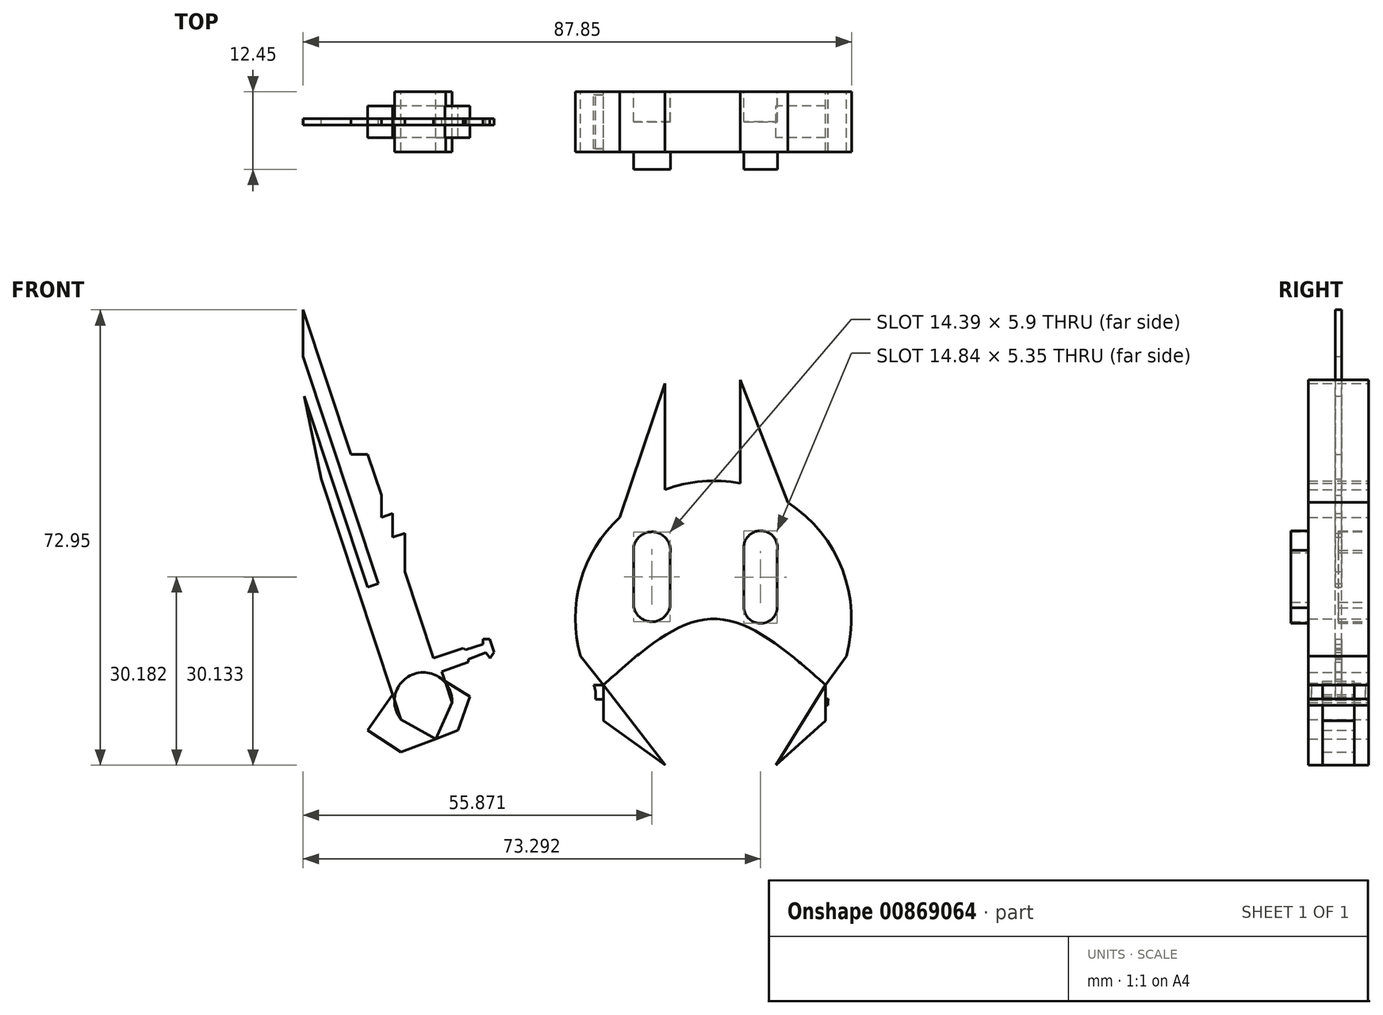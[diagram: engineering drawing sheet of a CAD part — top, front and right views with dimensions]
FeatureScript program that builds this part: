
annotation { "Feature Type Name" : "Feature", "Feature Type Description" : "" }
export const myFeature = defineFeature(function(context is Context, id is Id, definition is map)
    precondition{}
    {
        {
            var Q0;
            Q0=qCreatedBy(makeId("Front.planeOp"),FACE);
            var sketch = newSketch(context, id + "F0", { "sketchPlane" : qUnion([Q0])});
            skLineSegment(sketch, "E0.bottom", {"start": v(-15.76, 7.28) * mm, "end": v(19.82, 7.28) * mm});
            skLineSegment(sketch, "E0.left", {"start": v(-15.76, 7.28) * mm, "end": v(-15.76, 1.57) * mm});
            skLineSegment(sketch, "E0.right", {"start": v(19.82, 7.28) * mm, "end": v(19.82, 1.57) * mm});
            skLineSegment(sketch, "E1", {"start": v(-15.76, 7.28) * mm, "end": v(-19.45, 11.89) * mm});
            skLineSegment(sketch, "E2", {"start": v(23.14, 11.89) * mm, "end": v(19.82, 7.28) * mm});
            skArc(sketch, "E3", {"start": v(23.14, 11.89) * mm, "mid": v(1.84, 40) * mm, "end": v(-19.45, 11.89) * mm});
            skLineSegment(sketch, "E4", {"start": v(-5.9, 38.59) * mm, "end": v(-5.9, 55.58) * mm});
            skLineSegment(sketch, "E5", {"start": v(-5.9, 55.58) * mm, "end": v(-13.15, 34.14) * mm});
            skLineSegment(sketch, "E6", {"start": v(6.13, 39.57) * mm, "end": v(6.13, 56.13) * mm});
            skLineSegment(sketch, "E7", {"start": v(6.13, 56.13) * mm, "end": v(13.75, 36.51) * mm});
            skLineSegment(sketch, "E8", {"start": v(-39.06, 0) * mm, "end": v(-48.21, -3.47) * mm});
            skLineSegment(sketch, "E9", {"start": v(-48.21, -3.47) * mm, "end": v(-53.56, 0) * mm});
            skLineSegment(sketch, "E10", {"start": v(-37.15, 5.44) * mm, "end": v(-39.06, 0) * mm});
            skLineSegment(sketch, "E11", {"start": v(-48.21, 1.77) * mm, "end": v(-60.97, 40.27) * mm});
            skLineSegment(sketch, "E12", {"start": v(-60.97, 40.27) * mm, "end": v(-63.7, 53.56) * mm});
            skLineSegment(sketch, "E13", {"start": v(-63.7, 53.56) * mm, "end": v(-53.56, 22.96) * mm});
            skLineSegment(sketch, "E14", {"start": v(-53.56, 22.96) * mm, "end": v(-51.84, 23.53) * mm});
            skLineSegment(sketch, "E15", {"start": v(-51.84, 23.53) * mm, "end": v(-63.9, 59.88) * mm});
            skLineSegment(sketch, "E16", {"start": v(-63.9, 59.88) * mm, "end": v(-63.9, 67.38) * mm});
            skLineSegment(sketch, "E17", {"start": v(-63.9, 67.38) * mm, "end": v(-57.09, 46.85) * mm});
            skLineSegment(sketch, "E18", {"start": v(-57.09, 46.85) * mm, "end": v(-56.2, 44.2) * mm});
            skLineSegment(sketch, "E19", {"start": v(-56.2, 44.2) * mm, "end": v(-53.56, 44.2) * mm});
            skLineSegment(sketch, "E20", {"start": v(-40.03, 4.48) * mm, "end": v(-41.66, 9.4) * mm});
            skLineSegment(sketch, "E21", {"start": v(-38.25, 13.18) * mm, "end": v(-43.01, 11.6) * mm});
            skLineSegment(sketch, "E22", {"start": v(-43.01, 11.6) * mm, "end": v(-47.6, 25.43) * mm});
            skLineSegment(sketch, "E23", {"start": v(-47.6, 25.43) * mm, "end": v(-47.6, 31.62) * mm});
            skLineSegment(sketch, "E24", {"start": v(-47.6, 31.62) * mm, "end": v(-49.53, 30.98) * mm});
            skLineSegment(sketch, "E25", {"start": v(-49.53, 30.98) * mm, "end": v(-49.53, 34.75) * mm});
            skLineSegment(sketch, "E26", {"start": v(-49.53, 34.75) * mm, "end": v(-51.33, 34.15) * mm});
            skLineSegment(sketch, "E27", {"start": v(-51.33, 34.15) * mm, "end": v(-51.33, 37.7) * mm});
            skLineSegment(sketch, "E28", {"start": v(-51.33, 37.7) * mm, "end": v(-53.56, 44.2) * mm});
            skArc(sketch, "E29", {"start": v(-40.03, 4.48) * mm, "mid": v(-46.08, 9.06) * mm, "end": v(-48.21, 1.77) * mm});
            skLineSegment(sketch, "E30", {"start": v(-42.63, -1.36) * mm, "end": v(-40.03, 4.48) * mm});
            skLineSegment(sketch, "E31", {"start": v(-48.21, 1.77) * mm, "end": v(-42.63, -1.36) * mm});
            skLineSegment(sketch, "E32", {"start": v(-53.56, 0) * mm, "end": v(-49.52, 5.74) * mm});
            skLineSegment(sketch, "E33", {"start": v(-37.15, 5.44) * mm, "end": v(-41.66, 8.2) * mm});
            skArc(sketch, "E34", {"start": v(-10.97, 20.37) * mm, "mid": v(-7.92, 17.42) * mm, "end": v(-5.07, 20.56) * mm});
            skLineSegment(sketch, "E35", {"start": v(-10.97, 20.37) * mm, "end": v(-10.97, 28.85) * mm});
            skLineSegment(sketch, "E36", {"start": v(-5.07, 20.56) * mm, "end": v(-5.07, 28.48) * mm});
            skArc(sketch, "E37", {"start": v(-5.07, 28.48) * mm, "mid": v(-7.82, 31.8) * mm, "end": v(-10.97, 28.85) * mm});
            skArc(sketch, "E38", {"start": v(12.08, 28.85) * mm, "mid": v(9.4, 31.98) * mm, "end": v(6.73, 28.85) * mm});
            skLineSegment(sketch, "E39", {"start": v(6.73, 28.85) * mm, "end": v(6.73, 19.82) * mm});
            skLineSegment(sketch, "E40", {"start": v(12.08, 28.85) * mm, "end": v(12.08, 19.63) * mm});
            skArc(sketch, "E41", {"start": v(6.73, 19.82) * mm, "mid": v(9.31, 17.14) * mm, "end": v(12.08, 19.63) * mm});
            skLineSegment(sketch, "E42", {"start": v(-44.65, -2.12) * mm, "end": v(-42.94, -6.62) * mm});
            skLineSegment(sketch, "E43", {"start": v(-41.24, -0.83) * mm, "end": v(-39.86, -5.04) * mm});
            skCircle(sketch, "E44", {"center": v(-38.9, -10.87) * mm, "radius": 5.92 * mm});
            skCircle(sketch, "E45", {"center": v(-38.9, -10.87) * mm, "radius": 4.33 * mm});
            skCircle(sketch, "E46", {"center": v(-38.9, -10.87) * mm, "radius": 1.05 * mm});
            skFitSpline(sketch, "E47", {"points": [v(-15.76, 7.28) * mm, v(1.84, 17.87) * mm, v(19.82, 7.28) * mm], "startDerivative": vector(35.23, 31.82) * mm, "endDerivative": vector(35.93, -31.74) * mm});
            skCircle(sketch, "E48", {"center": v(-21.52, 5.6) * mm, "radius": 4.51 * mm});
            skLineSegment(sketch, "E49", {"start": v(-15.76, 7.28) * mm, "end": v(-17.33, 7.28) * mm});
            skLineSegment(sketch, "E50", {"start": v(-17.05, 4.97) * mm, "end": v(-15.76, 4.97) * mm});
            skCircle(sketch, "E51", {"center": v(-29.67, -1.68) * mm, "radius": 2.4 * mm});
            skLineSegment(sketch, "E52", {"start": v(-32.06, -1.6) * mm, "end": v(-36.48, -5.47) * mm});
            skLineSegment(sketch, "E53", {"start": v(-29.59, -4.07) * mm, "end": v(-33.65, -8.14) * mm});
            skLineSegment(sketch, "E54", {"start": v(-29.32, 0.7) * mm, "end": v(-25.92, 4.57) * mm});
            skLineSegment(sketch, "E55", {"start": v(-27.31, -1.22) * mm, "end": v(-23.42, 1.5) * mm});
            skCircle(sketch, "E56", {"center": v(-29.67, -1.68) * mm, "radius": 1.75 * mm});
            skCircle(sketch, "E57", {"center": v(-21.52, 5.6) * mm, "radius": 1.75 * mm});
            skLineSegment(sketch, "E58", {"start": v(-21.52, 5.6) * mm, "end": v(-23.27, 5.6) * mm});
            skLineSegment(sketch, "E59", {"start": v(-23.27, 5.6) * mm, "end": v(-28.85, -0.13) * mm});
            skLineSegment(sketch, "E60", {"start": v(-21.52, 5.6) * mm, "end": v(-21.52, 3.85) * mm});
            skLineSegment(sketch, "E61", {"start": v(-21.52, 3.85) * mm, "end": v(-28.06, -1) * mm});
            skLineSegment(sketch, "E62", {"start": v(-38.9, -10.87) * mm, "end": v(-38.9, -9.82) * mm});
            skLineSegment(sketch, "E63", {"start": v(-38.9, -9.82) * mm, "end": v(-31.28, -2.36) * mm});
            skLineSegment(sketch, "E64", {"start": v(-38.9, -10.87) * mm, "end": v(-37.85, -10.87) * mm});
            skLineSegment(sketch, "E65", {"start": v(-37.85, -10.87) * mm, "end": v(-30.38, -3.28) * mm});
            skLineSegment(sketch, "E66", {"start": v(-37.15, 5.44) * mm, "end": v(-32.36, 8.08) * mm});
            skLineSegment(sketch, "E67", {"start": v(-32.36, 8.08) * mm, "end": v(-39.06, 0) * mm});
            skLineSegment(sketch, "E68", {"start": v(-59.26, -0.64) * mm, "end": v(-48.21, -3.47) * mm});
            skLineSegment(sketch, "E69", {"start": v(-53.56, 0) * mm, "end": v(-59.26, -0.64) * mm});
            skLineSegment(sketch, "E70", {"start": v(-38.25, 13.18) * mm, "end": v(-37.87, 12.9) * mm});
            skLineSegment(sketch, "E71", {"start": v(-37.87, 12.9) * mm, "end": v(-35.08, 13.83) * mm});
            skLineSegment(sketch, "E72", {"start": v(-35.08, 13.83) * mm, "end": v(-35.08, 14.65) * mm});
            skLineSegment(sketch, "E73", {"start": v(-35.08, 14.65) * mm, "end": v(-33.97, 14.65) * mm});
            skLineSegment(sketch, "E74", {"start": v(-33.97, 14.65) * mm, "end": v(-33.27, 12.51) * mm});
            skLineSegment(sketch, "E75", {"start": v(-33.27, 12.51) * mm, "end": v(-33.9, 11.6) * mm});
            skLineSegment(sketch, "E76", {"start": v(-33.9, 11.6) * mm, "end": v(-34.63, 12.5) * mm});
            skLineSegment(sketch, "E77", {"start": v(-34.63, 12.5) * mm, "end": v(-37.4, 11.4) * mm});
            skLineSegment(sketch, "E78", {"start": v(-37.4, 11.4) * mm, "end": v(-37.4, 10.98) * mm});
            skLineSegment(sketch, "E79", {"start": v(-37.4, 10.98) * mm, "end": v(-41.66, 9.4) * mm});
            skCircle(sketch, "E80", {"center": v(33.96, -15.69) * mm, "radius": 5 * mm});
            skLineSegment(sketch, "E81", {"start": v(-15.76, 1.57) * mm, "end": v(-5.84, -5.57) * mm});
            skLineSegment(sketch, "E82", {"start": v(-5.84, -5.57) * mm, "end": v(11.89, -5.57) * mm});
            skLineSegment(sketch, "E83", {"start": v(11.89, -5.57) * mm, "end": v(19.82, 1.57) * mm});
            skLineSegment(sketch, "E84", {"start": v(-15.76, 7.28) * mm, "end": v(-5.84, -5.57) * mm});
            skLineSegment(sketch, "E85", {"start": v(19.82, 7.28) * mm, "end": v(11.89, -5.57) * mm});
            skLineSegment(sketch, "E86", {"start": v(25.44, 1.57) * mm, "end": v(25.18, 7.28) * mm});
            skLineSegment(sketch, "E87", {"start": v(-9.91, 12.56) * mm, "end": v(-6, 7.28) * mm});
            skLineSegment(sketch, "E88", {"start": v(13.8, 12.59) * mm, "end": v(9.34, 7.28) * mm});
            skLineSegment(sketch, "E89", {"start": v(25.18, 7.28) * mm, "end": v(30.14, 24.43) * mm});
            skLineSegment(sketch, "E90", {"start": v(30.14, 24.43) * mm, "end": v(32.94, 16.26) * mm});
            skArc(sketch, "E91", {"start": v(32.94, 16.26) * mm, "mid": v(27.23, 9.12) * mm, "end": v(33.8, 2.77) * mm});
            skLineSegment(sketch, "E92", {"start": v(33.8, 2.77) * mm, "end": v(33.8, -2.6) * mm});
            skCircle(sketch, "E93", {"center": v(22.55, 4.35) * mm, "radius": 2.39 * mm});
            skLineSegment(sketch, "E94", {"start": v(24.76, 5.25) * mm, "end": v(25.31, 5.28) * mm});
            skPoint(sketch, "E94.endSnap0", {"position": v(25.31, 4.42) * mm});
            skLineSegment(sketch, "E95", {"start": v(24.9, 3.98) * mm, "end": v(25.33, 4) * mm});
            skLineSegment(sketch, "E96", {"start": v(20.26, 5.03) * mm, "end": v(19.82, 5.03) * mm});
            skLineSegment(sketch, "E97", {"start": v(20.18, 4.02) * mm, "end": v(19.82, 4.02) * mm});
            skLineSegment(sketch, "E98", {"start": v(25.44, 1.57) * mm, "end": v(33.8, -2.6) * mm});
            skCircle(sketch, "E99", {"center": v(34, 9.56) * mm, "radius": 5.31 * mm});
            skLineSegment(sketch, "E100", {"start": v(28.72, 9.03) * mm, "end": v(27.23, 9.03) * mm});
            skLineSegment(sketch, "E101", {"start": v(28.78, 10.5) * mm, "end": v(27.28, 10.5) * mm});
            skArc(sketch, "E102", {"start": v(35.95, 10.39) * mm, "mid": v(34.13, 12.17) * mm, "end": v(32.23, 10.46) * mm});
            skLineSegment(sketch, "E103", {"start": v(32.23, 10.46) * mm, "end": v(32.23, -14.4) * mm});
            skLineSegment(sketch, "E104", {"start": v(32.23, -14.4) * mm, "end": v(33.96, -15.69) * mm});
            skLineSegment(sketch, "E105", {"start": v(33.96, -15.69) * mm, "end": v(35.7, -14.4) * mm});
            skLineSegment(sketch, "E106", {"start": v(35.7, -14.4) * mm, "end": v(35.95, 10.39) * mm});
            skArc(sketch, "E107", {"start": v(32.23, -14.4) * mm, "mid": v(33.96, -18.06) * mm, "end": v(35.7, -14.4) * mm});
            skLineSegment(sketch, "E108", {"start": v(35.2, -20.53) * mm, "end": v(35.2, -28.23) * mm});
            skLineSegment(sketch, "E109", {"start": v(32.87, -20.57) * mm, "end": v(32.87, -28.2) * mm});
            skLineSegment(sketch, "E110", {"start": v(39.5, -25.26) * mm, "end": v(35.95, -41.2) * mm});
            skLineSegment(sketch, "E111", {"start": v(28.5, -25.57) * mm, "end": v(24.97, -22.31) * mm});
            skLineSegment(sketch, "E112", {"start": v(24.97, -22.31) * mm, "end": v(26.4, -28.2) * mm});
            skLineSegment(sketch, "E113", {"start": v(26.4, -28.2) * mm, "end": v(29.95, -31.2) * mm});
            skLineSegment(sketch, "E114", {"start": v(39.5, -25.26) * mm, "end": v(43.36, -22.27) * mm});
            skLineSegment(sketch, "E115", {"start": v(43.36, -22.27) * mm, "end": v(41.75, -28.56) * mm});
            skLineSegment(sketch, "E116", {"start": v(41.75, -28.56) * mm, "end": v(38.35, -30.4) * mm});
            skLineSegment(sketch, "E117", {"start": v(28.5, -35.98) * mm, "end": v(32.54, -41.2) * mm});
            skLineSegment(sketch, "E118", {"start": v(39.54, -35.66) * mm, "end": v(35.95, -41.2) * mm});
            skCircle(sketch, "E119", {"center": v(34.07, -31.3) * mm, "radius": 2.67 * mm});
            skLineSegment(sketch, "E120", {"start": v(28.5, -25.57) * mm, "end": v(34.09, -22.67) * mm});
            skLineSegment(sketch, "E121", {"start": v(34.09, -22.67) * mm, "end": v(39.5, -25.26) * mm});
            skLineSegment(sketch, "E122", {"start": v(32.87, -28.2) * mm, "end": v(34.07, -31.3) * mm});
            skLineSegment(sketch, "E123", {"start": v(34.07, -31.3) * mm, "end": v(35.2, -28.23) * mm});
            skArc(sketch, "E124", {"start": v(33.68, -30.28) * mm, "mid": v(34.02, -32.42) * mm, "end": v(34.44, -30.3) * mm});
            skLineSegment(sketch, "E125", {"start": v(35.2, -28.23) * mm, "end": v(38.35, -30.4) * mm});
            skLineSegment(sketch, "E126", {"start": v(32.87, -28.2) * mm, "end": v(29.95, -31.2) * mm});
            skLineSegment(sketch, "E127", {"start": v(29.95, -31.2) * mm, "end": v(28.5, -35.98) * mm});
            skLineSegment(sketch, "E128", {"start": v(38.35, -30.4) * mm, "end": v(39.54, -35.66) * mm});
            skLineSegment(sketch, "E129", {"start": v(28.5, -25.57) * mm, "end": v(29.95, -31.2) * mm});
            skLineSegment(sketch, "E130", {"start": v(29.95, -31.2) * mm, "end": v(32.54, -41.2) * mm});
            skLineSegment(sketch, "E131", {"start": v(32.54, -41.2) * mm, "end": v(32.54, -41.85) * mm});
            skLineSegment(sketch, "E132", {"start": v(32.54, -41.85) * mm, "end": v(35.95, -41.85) * mm});
            skLineSegment(sketch, "E133", {"start": v(35.95, -41.85) * mm, "end": v(35.95, -41.2) * mm});
            skLineSegment(sketch, "E134", {"start": v(34.02, -37.9) * mm, "end": v(32.54, -41.2) * mm});
            skLineSegment(sketch, "E135", {"start": v(34.02, -37.9) * mm, "end": v(35.95, -41.2) * mm});
            skCircle(sketch, "E136", {"center": v(34.18, -43.8) * mm, "radius": 1.74 * mm});
            skLineSegment(sketch, "E137", {"start": v(32.86, -41.85) * mm, "end": v(32.86, -42.67) * mm});
            skLineSegment(sketch, "E138", {"start": v(33.2, -41.85) * mm, "end": v(33.2, -42.37) * mm});
            skLineSegment(sketch, "E139", {"start": v(33.93, -41.85) * mm, "end": v(33.93, -42.08) * mm});
            skLineSegment(sketch, "E140", {"start": v(34.32, -41.85) * mm, "end": v(34.32, -42.06) * mm});
            skLineSegment(sketch, "E141", {"start": v(35.06, -41.85) * mm, "end": v(35.06, -42.3) * mm});
            skLineSegment(sketch, "E142", {"start": v(35.42, -41.85) * mm, "end": v(35.42, -42.57) * mm});
            skLineSegment(sketch, "E143", {"start": v(31.7, -43.74) * mm, "end": v(31.7, -46.07) * mm});
            skLineSegment(sketch, "E144", {"start": v(31.7, -46.07) * mm, "end": v(36.58, -46.07) * mm});
            skLineSegment(sketch, "E145", {"start": v(36.58, -46.07) * mm, "end": v(36.58, -43.76) * mm});
            skLineSegment(sketch, "E146", {"start": v(33.9, -45.52) * mm, "end": v(33.9, -45.7) * mm});
            skLineSegment(sketch, "E147", {"start": v(34.48, -45.51) * mm, "end": v(34.48, -45.7) * mm});
            skLineSegment(sketch, "E148", {"start": v(31.7, -43.74) * mm, "end": v(32.14, -43.74) * mm});
            skLineSegment(sketch, "E149", {"start": v(36.58, -43.76) * mm, "end": v(36.19, -43.76) * mm});
            skLineSegment(sketch, "E150", {"start": v(32.47, -44.07) * mm, "end": v(32.14, -44.07) * mm});
            skLineSegment(sketch, "E151", {"start": v(32.54, -44.37) * mm, "end": v(32.14, -44.37) * mm});
            skLineSegment(sketch, "E152", {"start": v(35.91, -44) * mm, "end": v(36.2, -44) * mm});
            skLineSegment(sketch, "E153", {"start": v(32.14, -43.74) * mm, "end": v(32.14, -44.07) * mm});
            skArc(sketch, "E154", {"start": v(32.14, -44.37) * mm, "mid": v(32.8, -45.34) * mm, "end": v(33.9, -45.7) * mm});
            skLineSegment(sketch, "E155", {"start": v(35.86, -44.27) * mm, "end": v(36.2, -44.27) * mm});
            skLineSegment(sketch, "E156", {"start": v(36.19, -43.76) * mm, "end": v(36.2, -44) * mm});
            skArc(sketch, "E157", {"start": v(34.48, -45.7) * mm, "mid": v(35.58, -45.28) * mm, "end": v(36.2, -44.27) * mm});
            skLineSegment(sketch, "E158.4", {"start": v(32.84, -46.15) * mm, "end": v(35.8, -46.16) * mm});
            skLineSegment(sketch, "E159", {"start": v(32.95, -46.07) * mm, "end": v(32.95, -46.15) * mm});
            skLineSegment(sketch, "E160", {"start": v(33.2, -46.07) * mm, "end": v(33.2, -46.15) * mm});
            skLineSegment(sketch, "E161", {"start": v(33.55, -46.07) * mm, "end": v(33.55, -46.15) * mm});
            skLineSegment(sketch, "E162", {"start": v(33.86, -46.07) * mm, "end": v(33.86, -46.15) * mm});
            skLineSegment(sketch, "E163", {"start": v(34.1, -46.07) * mm, "end": v(34.1, -46.15) * mm});
            skLineSegment(sketch, "E164", {"start": v(34.36, -46.07) * mm, "end": v(34.36, -46.16) * mm});
            skLineSegment(sketch, "E165", {"start": v(34.65, -46.07) * mm, "end": v(34.65, -46.16) * mm});
            skLineSegment(sketch, "E166", {"start": v(34.92, -46.07) * mm, "end": v(34.92, -46.16) * mm});
            skLineSegment(sketch, "E167", {"start": v(35.18, -46.07) * mm, "end": v(35.18, -46.16) * mm});
            skLineSegment(sketch, "E168", {"start": v(35.46, -46.07) * mm, "end": v(35.46, -46.16) * mm});
            skLineSegment(sketch, "E169", {"start": v(35.62, -46.07) * mm, "end": v(35.62, -46.16) * mm});
            skLineSegment(sketch, "E170.0", {"start": v(38.42, -49.81) * mm, "end": v(36.32, -53.4) * mm});
            skLineSegment(sketch, "E170.1", {"start": v(36.32, -53.4) * mm, "end": v(32.17, -53.36) * mm});
            skLineSegment(sketch, "E170.2", {"start": v(32.17, -53.36) * mm, "end": v(30.12, -49.75) * mm});
            skLineSegment(sketch, "E170.3", {"start": v(30.12, -49.75) * mm, "end": v(32.22, -46.17) * mm});
            skLineSegment(sketch, "E170.4", {"start": v(32.22, -46.17) * mm, "end": v(36.37, -46.2) * mm});
            skLineSegment(sketch, "E170.5", {"start": v(36.37, -46.2) * mm, "end": v(38.42, -49.81) * mm});
            skPoint(sketch, "E170.0.midPoint", {"position": v(37.37, -51.6) * mm});
            skArc(sketch, "E171", {"start": v(30.12, -49.75) * mm, "mid": v(34.23, -54.9) * mm, "end": v(38.42, -49.81) * mm});
            skLineSegment(sketch, "E172", {"start": v(30.12, -49.75) * mm, "end": v(34.26, -50.65) * mm});
            skLineSegment(sketch, "E173", {"start": v(38.42, -49.81) * mm, "end": v(34.26, -50.65) * mm});
            skLineSegment(sketch, "E174", {"start": v(30.04, -51.06) * mm, "end": v(28.9, -51.7) * mm});
            skLineSegment(sketch, "E175", {"start": v(28.9, -51.7) * mm, "end": v(30.27, -52.09) * mm});
            skLineSegment(sketch, "E176", {"start": v(38.48, -51.12) * mm, "end": v(39.68, -51.78) * mm});
            skLineSegment(sketch, "E177", {"start": v(39.68, -51.78) * mm, "end": v(38.2, -52.22) * mm});
            skLineSegment(sketch, "E178", {"start": v(31.2, -53.6) * mm, "end": v(30.81, -54.98) * mm});
            skLineSegment(sketch, "E179", {"start": v(30.81, -54.98) * mm, "end": v(32.15, -54.33) * mm});
            skLineSegment(sketch, "E180", {"start": v(33.68, -54.85) * mm, "end": v(34.23, -56.04) * mm});
            skPoint(sketch, "E180.endSnap0", {"position": v(34.23, -54.9) * mm});
            skLineSegment(sketch, "E181", {"start": v(34.23, -56.04) * mm, "end": v(34.95, -54.84) * mm});
            skLineSegment(sketch, "E182", {"start": v(36.34, -54.35) * mm, "end": v(37.7, -55.15) * mm});
            skPoint(sketch, "E182.startSnap0", {"position": v(36.34, -50.23) * mm});
            skLineSegment(sketch, "E183", {"start": v(37.7, -55.15) * mm, "end": v(37.38, -53.53) * mm});
            skLineSegment(sketch, "E184.top", {"start": v(-5.84, -33.89) * mm, "end": v(12.35, -33.89) * mm});
            skLineSegment(sketch, "E184.left", {"start": v(-5.84, -30.08) * mm, "end": v(-5.84, -33.89) * mm});
            skLineSegment(sketch, "E184.right", {"start": v(12.35, -30.08) * mm, "end": v(12.35, -33.89) * mm});
            skLineSegment(sketch, "E185", {"start": v(-5.84, -30.08) * mm, "end": v(-11.43, -30.08) * mm});
            skLineSegment(sketch, "E186", {"start": v(-11.43, -30.08) * mm, "end": v(-5.84, -33.89) * mm});
            skLineSegment(sketch, "E187", {"start": v(12.35, -30.08) * mm, "end": v(18.1, -30.08) * mm});
            skLineSegment(sketch, "E188", {"start": v(18.1, -30.08) * mm, "end": v(12.35, -33.89) * mm});
            skCircle(sketch, "E189", {"center": v(3.02, -18.97) * mm, "radius": 6.33 * mm});
            skPoint(sketch, "E189.centerSnap0", {"position": v(3.02, -5.57) * mm});
            skLineSegment(sketch, "E190", {"start": v(-5.84, -5.57) * mm, "end": v(3.02, -18.97) * mm});
            skLineSegment(sketch, "E191", {"start": v(11.89, -5.57) * mm, "end": v(3.02, -18.97) * mm});
            skLineSegment(sketch, "E192", {"start": v(3.02, -18.97) * mm, "end": v(-5.84, -30.08) * mm});
            skLineSegment(sketch, "E193", {"start": v(3.02, -18.97) * mm, "end": v(12.35, -30.08) * mm});
            skPoint(sketch, "E194", {"position": v(-0.47, -13.7) * mm});
            skPoint(sketch, "E195", {"position": v(6.51, -13.7) * mm});
            skPoint(sketch, "E196", {"position": v(-0.93, -23.92) * mm});
            skPoint(sketch, "E197", {"position": v(7.1, -23.82) * mm});
            skPoint(sketch, "E198", {"position": v(3.25, -42.98) * mm});
            skArc(sketch, "E199", {"start": v(-5.84, -33.89) * mm, "mid": v(3.25, -42.98) * mm, "end": v(12.35, -33.89) * mm});
            skLineSegment(sketch, "E200", {"start": v(-9.7, -37.42) * mm, "end": v(-14.57, -53.8) * mm});
            skLineSegment(sketch, "E201", {"start": v(-14.57, -53.8) * mm, "end": v(-8.4, -55.63) * mm});
            skLineSegment(sketch, "E202", {"start": v(-8.4, -55.63) * mm, "end": v(0, -46) * mm});
            skArc(sketch, "E203", {"start": v(-9.7, -37.42) * mm, "mid": v(-6.49, -43.56) * mm, "end": v(0, -46) * mm});
            skCircle(sketch, "E204", {"center": v(-5.02, -41.77) * mm, "radius": 2.38 * mm});
            skCircle(sketch, "E205", {"center": v(3.34, -31.78) * mm, "radius": 2.83 * mm});
            skArc(sketch, "E206", {"start": v(5.13, -33.39) * mm, "mid": v(3.43, -31.79) * mm, "end": v(1.57, -33.2) * mm});
            skArc(sketch, "E207", {"start": v(5.13, -33.39) * mm, "mid": v(3.38, -32.7) * mm, "end": v(1.57, -33.2) * mm});
            skCircle(sketch, "E208", {"center": v(-13.17, -57.63) * mm, "radius": 2.28 * mm});
            skLineSegment(sketch, "E209", {"start": v(-17.2, -56) * mm, "end": v(-17.2, -71.94) * mm});
            skLineSegment(sketch, "E210", {"start": v(-8.84, -57.78) * mm, "end": v(-10.78, -72.54) * mm});
            skLineSegment(sketch, "E211", {"start": v(-17.2, -56) * mm, "end": v(-15.52, -60.13) * mm});
            skLineSegment(sketch, "E212", {"start": v(-15.52, -60.13) * mm, "end": v(-11.73, -60.9) * mm});
            skLineSegment(sketch, "E213", {"start": v(-11.73, -60.9) * mm, "end": v(-8.84, -57.78) * mm});
            skLineSegment(sketch, "E214", {"start": v(-13.32, -54.16) * mm, "end": v(-14.07, -55.54) * mm});
            skLineSegment(sketch, "E215", {"start": v(-13.12, -54.22) * mm, "end": v(-13.6, -55.39) * mm});
            skLineSegment(sketch, "E216", {"start": v(-11.96, -54.57) * mm, "end": v(-12.54, -55.44) * mm});
            skLineSegment(sketch, "E217", {"start": v(-11.42, -54.73) * mm, "end": v(-12.02, -55.66) * mm});
            skLineSegment(sketch, "E218", {"start": v(-10.6, -54.98) * mm, "end": v(-11.49, -56.09) * mm});
            skLineSegment(sketch, "E219", {"start": v(-10.3, -55.06) * mm, "end": v(-11.21, -56.46) * mm});
            skCircle(sketch, "E220", {"center": v(-13.17, -57.63) * mm, "radius": 0.68 * mm});
            skCircle(sketch, "E221", {"center": v(-14.33, -75.96) * mm, "radius": 3.36 * mm});
            skLineSegment(sketch, "E222", {"start": v(-17.2, -71.94) * mm, "end": v(-18.76, -73.06) * mm});
            skLineSegment(sketch, "E223", {"start": v(-18.76, -73.06) * mm, "end": v(-15.3, -71.94) * mm});
            skLineSegment(sketch, "E224", {"start": v(-15.3, -71.94) * mm, "end": v(-12.92, -71.94) * mm});
            skLineSegment(sketch, "E225", {"start": v(-12.92, -71.94) * mm, "end": v(-10.07, -73.28) * mm});
            skLineSegment(sketch, "E226", {"start": v(-10.07, -73.28) * mm, "end": v(-10.78, -72.54) * mm});
            skLineSegment(sketch, "E227", {"start": v(-17.2, -71.94) * mm, "end": v(-15.52, -60.13) * mm});
            skLineSegment(sketch, "E228", {"start": v(-11.73, -60.9) * mm, "end": v(-10.78, -72.54) * mm});
            skLineSegment(sketch, "E229", {"start": v(-15.3, -71.94) * mm, "end": v(-15.23, -72.72) * mm});
            skLineSegment(sketch, "E230", {"start": v(-14.98, -71.94) * mm, "end": v(-14.98, -72.65) * mm});
            skLineSegment(sketch, "E231", {"start": v(-14.41, -71.94) * mm, "end": v(-14.41, -72.6) * mm});
            skLineSegment(sketch, "E232", {"start": v(-14.1, -71.94) * mm, "end": v(-14.1, -72.6) * mm});
            skLineSegment(sketch, "E233", {"start": v(-12.92, -71.94) * mm, "end": v(-13.14, -72.81) * mm});
            skLineSegment(sketch, "E234", {"start": v(-13.36, -71.94) * mm, "end": v(-13.36, -72.74) * mm});
            skLineSegment(sketch, "E235", {"start": v(-17.7, -80.72) * mm, "end": v(-14.88, -80.72) * mm});
            skLineSegment(sketch, "E236", {"start": v(-14.88, -80.72) * mm, "end": v(-14.2, -79.32) * mm});
            skLineSegment(sketch, "E237", {"start": v(-14.2, -79.32) * mm, "end": v(-13.75, -80.68) * mm});
            skLineSegment(sketch, "E238", {"start": v(-13.75, -80.68) * mm, "end": v(-11.02, -80.68) * mm});
            skLineSegment(sketch, "E239", {"start": v(-15.18, -58.7) * mm, "end": v(-15.52, -60.13) * mm});
            skLineSegment(sketch, "E240", {"start": v(-14.7, -59.32) * mm, "end": v(-15.15, -60.2) * mm});
            skLineSegment(sketch, "E241", {"start": v(-13.95, -59.78) * mm, "end": v(-13.95, -60.45) * mm});
            skLineSegment(sketch, "E242", {"start": v(-13.3, -59.9) * mm, "end": v(-13.62, -60.51) * mm});
            skLineSegment(sketch, "E243", {"start": v(-12.48, -59.8) * mm, "end": v(-12.66, -60.7) * mm});
            skLineSegment(sketch, "E244", {"start": v(-11.9, -59.53) * mm, "end": v(-12.17, -60.8) * mm});
            skLineSegment(sketch, "E245", {"start": v(-17.7, -76.16) * mm, "end": v(-20.3, -80.77) * mm});
            skLineSegment(sketch, "E246", {"start": v(-20.3, -80.77) * mm, "end": v(-17.7, -80.72) * mm});
            skLineSegment(sketch, "E247", {"start": v(-11.02, -80.68) * mm, "end": v(-7.93, -80.72) * mm});
            skLineSegment(sketch, "E248", {"start": v(-7.93, -80.72) * mm, "end": v(-10.97, -76) * mm});
            skLineSegment(sketch, "E249", {"start": v(1.57, -30.46) * mm, "end": v(2.07, -30.8) * mm});
            skLineSegment(sketch, "E250", {"start": v(2.07, -30.8) * mm, "end": v(1.6, -31.48) * mm});
            skLineSegment(sketch, "E251", {"start": v(1.6, -31.48) * mm, "end": v(1.99, -31.75) * mm});
            skLineSegment(sketch, "E252", {"start": v(1.99, -31.75) * mm, "end": v(2.48, -31.04) * mm});
            skLineSegment(sketch, "E253", {"start": v(2.48, -31.04) * mm, "end": v(3.18, -31.53) * mm});
            skLineSegment(sketch, "E254", {"start": v(3.18, -31.53) * mm, "end": v(3.4, -31.21) * mm});
            skLineSegment(sketch, "E255", {"start": v(3.4, -31.21) * mm, "end": v(2.73, -30.74) * mm});
            skLineSegment(sketch, "E256", {"start": v(2.73, -30.74) * mm, "end": v(3.1, -30.2) * mm});
            skLineSegment(sketch, "E257", {"start": v(3.1, -30.2) * mm, "end": v(2.67, -29.9) * mm});
            skLineSegment(sketch, "E258", {"start": v(2.67, -29.9) * mm, "end": v(2.29, -30.45) * mm});
            skLineSegment(sketch, "E259", {"start": v(2.29, -30.45) * mm, "end": v(1.82, -30.13) * mm});
            skLineSegment(sketch, "E260", {"start": v(1.82, -30.13) * mm, "end": v(1.57, -30.46) * mm});
            skLineSegment(sketch, "E261", {"start": v(3.5, -30.25) * mm, "end": v(3.92, -29.83) * mm});
            skLineSegment(sketch, "E262", {"start": v(3.92, -29.83) * mm, "end": v(4.51, -30.43) * mm});
            skLineSegment(sketch, "E263", {"start": v(4.51, -30.43) * mm, "end": v(5.1, -29.85) * mm});
            skLineSegment(sketch, "E264", {"start": v(5.1, -29.85) * mm, "end": v(5.47, -30.23) * mm});
            skLineSegment(sketch, "E265", {"start": v(5.47, -30.23) * mm, "end": v(4.88, -30.82) * mm});
            skLineSegment(sketch, "E266", {"start": v(4.88, -30.82) * mm, "end": v(5.51, -31.45) * mm});
            skLineSegment(sketch, "E267", {"start": v(5.51, -31.45) * mm, "end": v(5.08, -31.87) * mm});
            skLineSegment(sketch, "E268", {"start": v(5.08, -31.87) * mm, "end": v(4.43, -31.22) * mm});
            skLineSegment(sketch, "E269", {"start": v(4.43, -31.22) * mm, "end": v(3.93, -31.71) * mm});
            skLineSegment(sketch, "E270", {"start": v(3.93, -31.71) * mm, "end": v(3.59, -31.26) * mm});
            skLineSegment(sketch, "E271", {"start": v(3.59, -31.26) * mm, "end": v(4.04, -30.8) * mm});
            skLineSegment(sketch, "E272", {"start": v(4.04, -30.8) * mm, "end": v(3.5, -30.25) * mm});
            skLineSegment(sketch, "E273", {"start": v(-5.84, -30.08) * mm, "end": v(1.07, -30.08) * mm});
            skLineSegment(sketch, "E274", {"start": v(12.35, -30.08) * mm, "end": v(5.6, -30.08) * mm});
            skLineSegment(sketch, "E275.MirrorCS", {"start": v(21.09, -71.84) * mm, "end": v(21.1, -72.5) * mm});
            skLineSegment(sketch, "E276.MirrorCS", {"start": v(19.08, -59.72) * mm, "end": v(19.27, -60.62) * mm});
            skLineSegment(sketch, "E277.MirrorCS", {"start": v(21.97, -71.84) * mm, "end": v(21.9, -72.6) * mm});
            skLineSegment(sketch, "E278.MirrorCS", {"start": v(21.78, -58.6) * mm, "end": v(22.12, -60.02) * mm});
            skLineSegment(sketch, "E279.MirrorCS", {"start": v(21.3, -59.22) * mm, "end": v(21.75, -60.1) * mm});
            skLineSegment(sketch, "E280.MirrorCS", {"start": v(20.78, -71.84) * mm, "end": v(20.78, -72.5) * mm});
            skLineSegment(sketch, "E281.MirrorCS", {"start": v(20.04, -71.85) * mm, "end": v(20.04, -72.64) * mm});
            skLineSegment(sketch, "E282.MirrorCS", {"start": v(18.5, -59.45) * mm, "end": v(18.77, -60.72) * mm});
            skLineSegment(sketch, "E283.MirrorCS", {"start": v(21.97, -71.84) * mm, "end": v(19.6, -71.85) * mm});
            skLineSegment(sketch, "E284.MirrorCS", {"start": v(21.65, -71.84) * mm, "end": v(21.65, -72.55) * mm});
            skLineSegment(sketch, "E285.MirrorCS", {"start": v(19.6, -71.85) * mm, "end": v(16.75, -73.2) * mm});
            skLineSegment(sketch, "E286.MirrorCS", {"start": v(19.6, -71.85) * mm, "end": v(19.82, -72.72) * mm});
            skLineSegment(sketch, "E287.MirrorCS", {"start": v(22.12, -60.02) * mm, "end": v(18.34, -60.81) * mm});
            skLineSegment(sketch, "E288.MirrorCS", {"start": v(25.44, -72.93) * mm, "end": v(21.97, -71.84) * mm});
            skLineSegment(sketch, "E289.MirrorCS", {"start": v(16.75, -73.2) * mm, "end": v(17.46, -72.46) * mm});
            skLineSegment(sketch, "E290.MirrorCS", {"start": v(19.9, -59.81) * mm, "end": v(20.23, -60.42) * mm});
            skLineSegment(sketch, "E291.MirrorCS", {"start": v(20.55, -59.68) * mm, "end": v(20.56, -60.35) * mm});
            skLineSegment(sketch, "E292.MirrorCS", {"start": v(23.87, -71.82) * mm, "end": v(25.44, -72.93) * mm});
            skCircle(sketch, "E293.MirrorC", {"center": v(19.76, -57.54) * mm, "radius": 0.68 * mm});
            skLineSegment(sketch, "E294.MirrorCS", {"start": v(19.7, -54.13) * mm, "end": v(20.17, -55.3) * mm});
            skLineSegment(sketch, "E295.MirrorCS", {"start": v(19.89, -54.07) * mm, "end": v(20.65, -55.44) * mm});
            skLineSegment(sketch, "E296.MirrorCS", {"start": v(24.42, -80.6) * mm, "end": v(21.6, -80.61) * mm});
            skLineSegment(sketch, "E297.MirrorCS", {"start": v(18, -54.64) * mm, "end": v(18.6, -55.57) * mm});
            skLineSegment(sketch, "E298.MirrorCS", {"start": v(20.93, -79.22) * mm, "end": v(20.47, -80.58) * mm});
            skLineSegment(sketch, "E299.MirrorCS", {"start": v(17.74, -80.6) * mm, "end": v(14.65, -80.65) * mm});
            skLineSegment(sketch, "E300.MirrorCS", {"start": v(17.17, -54.9) * mm, "end": v(18.07, -56) * mm});
            skLineSegment(sketch, "E301.MirrorCS", {"start": v(21.13, -53.69) * mm, "end": v(14.97, -55.56) * mm});
            skLineSegment(sketch, "E302.MirrorCS", {"start": v(16.88, -54.98) * mm, "end": v(17.8, -56.37) * mm});
            skLineSegment(sketch, "E303.MirrorCS", {"start": v(21.6, -80.61) * mm, "end": v(20.93, -79.22) * mm});
            skLineSegment(sketch, "E304.MirrorCS", {"start": v(20.47, -80.58) * mm, "end": v(17.74, -80.6) * mm});
            skLineSegment(sketch, "E305.MirrorCS", {"start": v(18.53, -54.48) * mm, "end": v(19.12, -55.35) * mm});
            skLineSegment(sketch, "E306.MirrorCS", {"start": v(27.02, -80.63) * mm, "end": v(24.42, -80.6) * mm});
            skCircle(sketch, "E307.MirrorC", {"center": v(19.76, -57.54) * mm, "radius": 2.28 * mm});
            skLineSegment(sketch, "E308.MirrorCS", {"start": v(23.77, -55.87) * mm, "end": v(22.12, -60.02) * mm});
            skLineSegment(sketch, "E309.MirrorCS", {"start": v(14.97, -55.56) * mm, "end": v(6.52, -45.98) * mm});
            skLineSegment(sketch, "E310.MirrorCS", {"start": v(18.34, -60.81) * mm, "end": v(15.44, -57.71) * mm});
            skLineSegment(sketch, "E311.MirrorCS", {"start": v(23.87, -71.82) * mm, "end": v(22.12, -60.02) * mm});
            skCircle(sketch, "E312.MirrorC", {"center": v(21.03, -75.85) * mm, "radius": 3.36 * mm});
            skLineSegment(sketch, "E313.MirrorCS", {"start": v(16.17, -37.35) * mm, "end": v(21.13, -53.69) * mm});
            skArc(sketch, "E314.MirrorCS", {"start": v(16.17, -37.35) * mm, "mid": v(13, -43.5) * mm, "end": v(6.52, -45.98) * mm});
            skLineSegment(sketch, "E315.MirrorCS", {"start": v(14.65, -80.65) * mm, "end": v(17.67, -75.91) * mm});
            skLineSegment(sketch, "E316.MirrorCS", {"start": v(24.39, -76.04) * mm, "end": v(27.02, -80.63) * mm});
            skLineSegment(sketch, "E317.MirrorCS", {"start": v(15.44, -57.71) * mm, "end": v(17.46, -72.46) * mm});
            skLineSegment(sketch, "E318.MirrorCS", {"start": v(23.77, -55.87) * mm, "end": v(23.87, -71.82) * mm});
            skLineSegment(sketch, "E319.MirrorCS", {"start": v(18.34, -60.81) * mm, "end": v(17.46, -72.46) * mm});
            skCircle(sketch, "E320.MirrorC", {"center": v(11.52, -41.73) * mm, "radius": 2.38 * mm});
            skSolve(sketch);
        }
        {
            var Q0;
            Q0=makeQuery(id+"F0.imprint","IMPRINT",FACE,{"disambiguationData":[TD([[makeQuery(id+"F0.imprint","IMPRINT",EDGE,{"derivedFrom":sQuery(id+"F0.wireOp",EDGE,"E34")}),-1.0]])]});
            var Q1;
            {var subQ0=sQuery(id+"F0.wireOp",EDGE,"E6");Q1=makeQuery(id+"F0.imprint","IMPRINT",FACE,{"disambiguationData":[TD([[makeQuery(id+"F0.imprint","IMPRINT",EDGE,{"derivedFrom":subQ0}),-1.0]])]});}
            var Q2;
            {var subQ0=sQuery(id+"F0.wireOp",EDGE,"E4");Q2=makeQuery(id+"F0.imprint","IMPRINT",FACE,{"disambiguationData":[TD([[makeQuery(id+"F0.imprint","IMPRINT",EDGE,{"derivedFrom":subQ0}),1.0]])]});}
            var Q3;
            {var subQ5=sQuery(id+"F0.wireOp",EDGE,"E0.right");Q3=makeQuery(id+"F0.imprint","IMPRINT",FACE,{"disambiguationData":[TD([[makeQuery(id+"F0.imprint","IMPRINT",EDGE,{"derivedFrom":subQ5}),1.0]])]});}
            var Q4;
            {var subQ0=sQuery(id+"F0.wireOp",EDGE,"Yl7WhlTw-apYZ-ukWC-n3tt-98KdLUmpt8E7");var subQ1=sQuery(id+"F0.wireOp",EDGE,"yNH20HZv-yYwh-2LKZ-svyh-G2NepNTWeq7k");var subQ2=makeQuery(id+"F0.imprint","INTERSECT",VERTEX,{"derivedFrom":[subQ1,subQ0]});Q4=makeQuery(id+"F0.imprint","IMPRINT",FACE,{"disambiguationData":[TD([[makeQuery(id+"F0.imprint","IMPRINT",EDGE,{"disambiguationData":[TD([[subQ2,1.0]])],"derivedFrom":subQ1}),-1.0]])]});}
            var Q5;
            {var subQ0=sQuery(id+"F0.wireOp",EDGE,"5KItvzyT-wADU-oRas-RmJE-PM86KJ7EwiFo");var subQ3=sQuery(id+"F0.wireOp",EDGE,"gnJdCNve-OrY5-z5BQ-lT9B-kEFE6d3iXY1r");var subQ5=makeQuery(id+"F0.imprint","INTERSECT",VERTEX,{"derivedFrom":[subQ0,subQ3]});Q5=makeQuery(id+"F0.imprint","IMPRINT",FACE,{"disambiguationData":[TD([[makeQuery(id+"F0.imprint","IMPRINT",EDGE,{"disambiguationData":[TD([[subQ5,1.0]])],"derivedFrom":subQ3}),1.0]])]});}
            var Q6;
            {var subQ0=sQuery(id+"F0.wireOp",EDGE,"T4VZFPXg-O3Kg-NQa6-04Wj-7CHUIA4H9gec");Q6=makeQuery(id+"F0.imprint","IMPRINT",FACE,{"disambiguationData":[TD([[makeQuery(id+"F0.imprint","IMPRINT",EDGE,{"derivedFrom":subQ0}),-1.0]])]});}
            var Q7;
            {var subQ0=sQuery(id+"F0.wireOp",EDGE,"5da51b9d-8d32-4ced-8ef7-5cde5154bd8f");var subQ2=sQuery(id+"F0.wireOp",EDGE,"c4sJ5hHI-HrM4-fpc8-U7ZW-TC2As1xjlsWM");var subQ3=makeQuery(id+"F0.imprint","INTERSECT",VERTEX,{"derivedFrom":[subQ2,subQ0]});Q7=makeQuery(id+"F0.imprint","IMPRINT",FACE,{"disambiguationData":[TD([[makeQuery(id+"F0.imprint","IMPRINT",EDGE,{"disambiguationData":[TD([[subQ3,1.0]])],"derivedFrom":subQ2}),-1.0]])]});}
            var Q8;
            {var subQ0=sQuery(id+"F0.wireOp",EDGE,"5da51b9d-8d32-4ced-8ef7-5cde5154bd8f");var subQ1=sQuery(id+"F0.wireOp",EDGE,"c4sJ5hHI-HrM4-fpc8-U7ZW-TC2As1xjlsWM");var subQ7=makeQuery(id+"F0.imprint","INTERSECT",VERTEX,{"derivedFrom":[subQ1,subQ0]});Q8=makeQuery(id+"F0.imprint","IMPRINT",FACE,{"disambiguationData":[TD([[makeQuery(id+"F0.imprint","IMPRINT",EDGE,{"disambiguationData":[TD([[subQ7,-1.0]])],"derivedFrom":subQ1}),-1.0]])]});}
            var Q9;
            {var subQ1=sQuery(id+"F0.wireOp",EDGE,"8bbff9a0-f29a-4255-a7a3-932c1e6babc1.1");var subQ7=makeQuery(id+"F0.imprint","INTERSECT",VERTEX,{"derivedFrom":[sQuery(id+"F0.wireOp",EDGE,"GHscTnbL-A1D7-kmX4-dKDm-pq0bj8ebfDfY"),subQ1]});Q9=makeQuery(id+"F0.imprint","IMPRINT",FACE,{"disambiguationData":[TD([[makeQuery(id+"F0.imprint","IMPRINT",EDGE,{"disambiguationData":[TD([[subQ7,-1.0]])],"derivedFrom":subQ1}),1.0]])]});}
            var Q10;
            {var subQ1=sQuery(id+"F0.wireOp",EDGE,"HR7Vcqbq-5GC2-dnc4-iXz6-dvDuRuYr12mq");var subQ7=sQuery(id+"F0.wireOp",EDGE,"RLhMJPxt-T0ks-Q18N-HPs9-RlDWo5XNaPYv");var subQ10=makeQuery(id+"F0.imprint","INTERSECT",VERTEX,{"derivedFrom":[subQ7,subQ1]});Q10=makeQuery(id+"F0.imprint","IMPRINT",FACE,{"disambiguationData":[TD([[makeQuery(id+"F0.imprint","IMPRINT",EDGE,{"disambiguationData":[TD([[subQ10,-1.0]])],"derivedFrom":subQ1}),1.0]])]});}
            var Q11;
            {var subQ0=sQuery(id+"F0.wireOp",EDGE,"xbz5I5cg-mLEk-vWxP-3GDN-i6KnoVRDJ0Sn");var subQ1=sQuery(id+"F0.wireOp",EDGE,"HR7Vcqbq-5GC2-dnc4-iXz6-dvDuRuYr12mq");var subQ2=makeQuery(id+"F0.imprint","INTERSECT",VERTEX,{"derivedFrom":[subQ1,subQ0]});Q11=makeQuery(id+"F0.imprint","IMPRINT",FACE,{"disambiguationData":[TD([[makeQuery(id+"F0.imprint","IMPRINT",EDGE,{"disambiguationData":[TD([[subQ2,-1.0]])],"derivedFrom":subQ1}),-1.0]])]});}
            var Q12;
            {var subQ3=sQuery(id+"F0.wireOp",EDGE,"95b7a578-6bee-43eb-946b-d34cbbbfe364");var subQ5=makeQuery(id+"F0.imprint","INTERSECT",VERTEX,{"derivedFrom":[sQuery(id+"F0.wireOp",EDGE,"xbz5I5cg-mLEk-vWxP-3GDN-i6KnoVRDJ0Sn"),subQ3]});Q12=makeQuery(id+"F0.imprint","IMPRINT",FACE,{"disambiguationData":[TD([[makeQuery(id+"F0.imprint","IMPRINT",EDGE,{"disambiguationData":[TD([[subQ5,1.0]])],"derivedFrom":subQ3}),-1.0]])]});}
            var Q13;
            Q13=makeQuery(id+"F0.imprint","IMPRINT",FACE,{"disambiguationData":[TD([[makeQuery(id+"F0.imprint","IMPRINT",EDGE,{"derivedFrom":sQuery(id+"F0.wireOp",EDGE,"fbyWGfAj-2cUi-kHPX-FlO8-zbxfvkLWJ3iW.bottom")}),1.0]])]});
            var Q14;
            {var subQ0=sQuery(id+"F0.wireOp",EDGE,"vNy1ZseG-UdZe-uj16-jnw9-NUYqMvN8ZLku.bottom");Q14=makeQuery(id+"F0.imprint","IMPRINT",FACE,{"disambiguationData":[TD([[makeQuery(id+"F0.imprint","IMPRINT",EDGE,{"derivedFrom":subQ0}),-1.0]])]});}
            var Q15;
            Q15=makeQuery(id+"F0.imprint","IMPRINT",FACE,{"disambiguationData":[TD([[makeQuery(id+"F0.imprint","IMPRINT",EDGE,{"derivedFrom":sQuery(id+"F0.wireOp",EDGE,"BFt47Mr2-YepH-lEwq-loFK-p4g8AKJxHlnc.bottom")}),1.0]])]});
            var Q16;
            Q16=makeQuery(id+"F0.imprint","IMPRINT",FACE,{"disambiguationData":[TD([[makeQuery(id+"F0.imprint","IMPRINT",EDGE,{"derivedFrom":sQuery(id+"F0.wireOp",EDGE,"UPGkduna-jT0j-80hk-QEkP-j2eCR6CrB44f.bottom")}),-1.0]])]});
            var Q17;
            {var subQ0=sQuery(id+"F0.wireOp",EDGE,"3ciVGj9d-eeR4-hxdk-o1da-vjnVaAnPwfeC");Q17=makeQuery(id+"F0.imprint","IMPRINT",FACE,{"disambiguationData":[TD([[makeQuery(id+"F0.imprint","IMPRINT",EDGE,{"derivedFrom":subQ0}),1.0]])]});}
            var Q18;
            {var subQ0=sQuery(id+"F0.wireOp",EDGE,"qswfnjLO-AV5f-Gmnw-SLyG-ogqKcAOzVCr5");Q18=makeQuery(id+"F0.imprint","IMPRINT",FACE,{"disambiguationData":[TD([[makeQuery(id+"F0.imprint","IMPRINT",EDGE,{"derivedFrom":subQ0}),1.0]])]});}
            var Q19;
            {var subQ0=sQuery(id+"F0.wireOp",EDGE,"AkOdhkDy-MqWK-eFBs-iVP6-e02GDzvXN1Q8");Q19=makeQuery(id+"F0.imprint","IMPRINT",FACE,{"disambiguationData":[TD([[makeQuery(id+"F0.imprint","IMPRINT",EDGE,{"derivedFrom":subQ0}),1.0]])]});}
            var Q20;
            {var subQ9=sQuery(id+"F0.wireOp",EDGE,"vNy1ZseG-UdZe-uj16-jnw9-NUYqMvN8ZLku.top");Q20=makeQuery(id+"F0.imprint","IMPRINT",FACE,{"disambiguationData":[TD([[makeQuery(id+"F0.imprint","IMPRINT",EDGE,{"derivedFrom":subQ9}),-1.0]])]});}
            var Q21;
            {var subQ5=sQuery(id+"F0.wireOp",EDGE,"E2");Q21=makeQuery(id+"F0.imprint","IMPRINT",FACE,{"disambiguationData":[TD([[makeQuery(id+"F0.imprint","IMPRINT",EDGE,{"derivedFrom":subQ5}),-1.0]])]});}
            var Q22;
            {var subQ0=sQuery(id+"F0.wireOp",EDGE,"8bbff9a0-f29a-4255-a7a3-932c1e6babc1.4");var subQ1=sQuery(id+"F0.wireOp",EDGE,"GHscTnbL-A1D7-kmX4-dKDm-pq0bj8ebfDfY");var subQ2=makeQuery(id+"F0.imprint","INTERSECT",VERTEX,{"derivedFrom":[subQ1,subQ0]});Q22=makeQuery(id+"F0.imprint","IMPRINT",FACE,{"disambiguationData":[TD([[makeQuery(id+"F0.imprint","IMPRINT",EDGE,{"disambiguationData":[TD([[subQ2,-1.0]])],"derivedFrom":subQ1}),-1.0]])]});}
            var Q23;
            {var subQ0=sQuery(id+"F0.wireOp",EDGE,"8bbff9a0-f29a-4255-a7a3-932c1e6babc1.3");var subQ1=sQuery(id+"F0.wireOp",EDGE,"GHscTnbL-A1D7-kmX4-dKDm-pq0bj8ebfDfY");var subQ2=makeQuery(id+"F0.imprint","INTERSECT",VERTEX,{"derivedFrom":[subQ1,subQ0]});Q23=makeQuery(id+"F0.imprint","IMPRINT",FACE,{"disambiguationData":[TD([[makeQuery(id+"F0.imprint","IMPRINT",EDGE,{"disambiguationData":[TD([[subQ2,-1.0]])],"derivedFrom":subQ1}),-1.0]])]});}
            var Q24;
            {var subQ0=sQuery(id+"F0.wireOp",EDGE,"7CLIC4A7-fy1N-yPjE-ywJT-88etpLGP96qZ");var subQ1=sQuery(id+"F0.wireOp",EDGE,"GHscTnbL-A1D7-kmX4-dKDm-pq0bj8ebfDfY");var subQ2=makeQuery(id+"F0.imprint","INTERSECT",VERTEX,{"derivedFrom":[subQ1,subQ0]});Q24=makeQuery(id+"F0.imprint","IMPRINT",FACE,{"disambiguationData":[TD([[makeQuery(id+"F0.imprint","IMPRINT",EDGE,{"disambiguationData":[TD([[subQ2,1.0]])],"derivedFrom":subQ1}),-1.0]])]});}
            var Q25;
            {var subQ0=sQuery(id+"F0.wireOp",EDGE,"7CLIC4A7-fy1N-yPjE-ywJT-88etpLGP96qZ");var subQ1=sQuery(id+"F0.wireOp",EDGE,"GHscTnbL-A1D7-kmX4-dKDm-pq0bj8ebfDfY");var subQ2=makeQuery(id+"F0.imprint","INTERSECT",VERTEX,{"derivedFrom":[subQ1,subQ0]});Q25=makeQuery(id+"F0.imprint","IMPRINT",FACE,{"disambiguationData":[TD([[makeQuery(id+"F0.imprint","IMPRINT",EDGE,{"disambiguationData":[TD([[subQ2,-1.0]])],"derivedFrom":subQ1}),-1.0]])]});}
            var Q26;
            {var subQ0=sQuery(id+"F0.wireOp",EDGE,"8bbff9a0-f29a-4255-a7a3-932c1e6babc1.0");var subQ1=sQuery(id+"F0.wireOp",EDGE,"GHscTnbL-A1D7-kmX4-dKDm-pq0bj8ebfDfY");var subQ2=makeQuery(id+"F0.imprint","INTERSECT",VERTEX,{"derivedFrom":[subQ1,subQ0]});Q26=makeQuery(id+"F0.imprint","IMPRINT",FACE,{"disambiguationData":[TD([[makeQuery(id+"F0.imprint","IMPRINT",EDGE,{"disambiguationData":[TD([[subQ2,1.0]])],"derivedFrom":subQ1}),-1.0]])]});}
            var Q27;
            {var subQ1=sQuery(id+"F0.wireOp",EDGE,"E0.top");var subQ3=sQuery(id+"F0.wireOp",EDGE,"8bbff9a0-f29a-4255-a7a3-932c1e6babc1.0");var subQ4=makeQuery(id+"F0.imprint","INTERSECT",VERTEX,{"derivedFrom":[subQ1,subQ3]});Q27=makeQuery(id+"F0.imprint","IMPRINT",FACE,{"disambiguationData":[TD([[makeQuery(id+"F0.imprint","IMPRINT",EDGE,{"disambiguationData":[TD([[subQ4,-1.0]])],"derivedFrom":subQ3}),-1.0]])]});}
            var Q28;
            {var subQ1=sQuery(id+"F0.wireOp",EDGE,"E1");Q28=makeQuery(id+"F0.imprint","IMPRINT",FACE,{"disambiguationData":[TD([[makeQuery(id+"F0.imprint","IMPRINT",EDGE,{"derivedFrom":subQ1}),-1.0]])]});}
            var Q29;
            {var subQ5=sQuery(id+"F0.wireOp",EDGE,"E0.left");Q29=makeQuery(id+"F0.imprint","IMPRINT",FACE,{"disambiguationData":[TD([[makeQuery(id+"F0.imprint","IMPRINT",EDGE,{"derivedFrom":subQ5}),1.0]])]});}
            var Q30;
            {var subQ4=sQuery(id+"F0.wireOp",EDGE,"7kdeA0x9-WurB-iCYt-142v-Vkt64plX1ea9");Q30=makeQuery(id+"F0.imprint","IMPRINT",FACE,{"disambiguationData":[TD([[makeQuery(id+"F0.imprint","IMPRINT",EDGE,{"derivedFrom":subQ4}),1.0]])]});}
            var Q31;
            {var subQ4=sQuery(id+"F0.wireOp",EDGE,"11D39QTh-0MAi-6cIM-IguO-1xuGzpaho9Pb");Q31=makeQuery(id+"F0.imprint","IMPRINT",FACE,{"disambiguationData":[TD([[makeQuery(id+"F0.imprint","IMPRINT",EDGE,{"derivedFrom":subQ4}),1.0]])]});}
            var Q32;
            {var subQ0=sQuery(id+"F0.wireOp",EDGE,"077caab9-3edd-4d49-a446-deb494107614");var subQ1=sQuery(id+"F0.wireOp",EDGE,"oO86CIyH-V04x-DpEi-sI8J-O24Eu7E0Mc1g");var subQ2=makeQuery(id+"F0.imprint","INTERSECT",VERTEX,{"disambiguationData":[OD(0.0)],"derivedFrom":[subQ1,subQ0]});Q32=makeQuery(id+"F0.imprint","IMPRINT",FACE,{"disambiguationData":[TD([[makeQuery(id+"F0.imprint","IMPRINT",EDGE,{"disambiguationData":[TD([[subQ2,-1.0]])],"derivedFrom":subQ1}),-1.0]])]});}
            var Q33;
            {var subQ1=sQuery(id+"F0.wireOp",EDGE,"717999c0-e526-4600-acb4-851d2ec1bb17");var subQ8=makeQuery(id+"F0.imprint","INTERSECT",VERTEX,{"derivedFrom":[subQ1,sQuery(id+"F0.wireOp",EDGE,"cJxqukpS-sKDF-N0Gn-XzKz-uhADJrMwIFSU")]});Q33=makeQuery(id+"F0.imprint","IMPRINT",FACE,{"disambiguationData":[TD([[makeQuery(id+"F0.imprint","IMPRINT",EDGE,{"disambiguationData":[TD([[subQ8,1.0]])],"derivedFrom":subQ1}),-1.0]])]});}
            var Q34;
            {var subQ1=sQuery(id+"F0.wireOp",EDGE,"47ef4d44-d683-4d7c-842c-7065e242f6f2");var subQ7=makeQuery(id+"F0.imprint","INTERSECT",VERTEX,{"derivedFrom":[subQ1,sQuery(id+"F0.wireOp",EDGE,"hjrOhq4C-YDQ2-2L1C-Vmbz-qUVbdpo7c3ap")]});Q34=makeQuery(id+"F0.imprint","IMPRINT",FACE,{"disambiguationData":[TD([[makeQuery(id+"F0.imprint","IMPRINT",EDGE,{"disambiguationData":[TD([[subQ7,1.0]])],"derivedFrom":subQ1}),1.0]])]});}
            var Q35;
            {var subQ0=sQuery(id+"F0.wireOp",EDGE,"5c1e8897-ab0d-4a54-afd1-e530e8574c37");Q35=makeQuery(id+"F0.imprint","IMPRINT",FACE,{"disambiguationData":[TD([[makeQuery(id+"F0.imprint","IMPRINT",EDGE,{"derivedFrom":subQ0}),1.0]])]});}
            var Q36;
            {var subQ0=sQuery(id+"F0.wireOp",EDGE,"E31");Q36=makeQuery(id+"F0.imprint","IMPRINT",FACE,{"disambiguationData":[TD([[makeQuery(id+"F0.imprint","IMPRINT",EDGE,{"derivedFrom":subQ0}),1.0]])]});}
            var Q37;
            {var subQ0=sQuery(id+"F0.wireOp",EDGE,"E30");Q37=makeQuery(id+"F0.imprint","IMPRINT",FACE,{"disambiguationData":[TD([[makeQuery(id+"F0.imprint","IMPRINT",EDGE,{"derivedFrom":subQ0}),1.0]])]});}
            var Q38;
            {var subQ0=sQuery(id+"F0.wireOp",EDGE,"E29");var subQ9=makeQuery(id+"F0.imprint","INTERSECT",VERTEX,{"derivedFrom":[subQ0,sQuery(id+"F0.wireOp",EDGE,"E33")]});Q38=makeQuery(id+"F0.imprint","IMPRINT",FACE,{"disambiguationData":[TD([[makeQuery(id+"F0.imprint","IMPRINT",EDGE,{"disambiguationData":[TD([[subQ9,1.0]])],"derivedFrom":subQ0}),1.0]])]});}
            var Q39;
            {var subQ0=sQuery(id+"F0.wireOp",EDGE,"f45a8b09-8381-489b-a60a-99bbd61589e0");var subQ1=sQuery(id+"F0.wireOp",EDGE,"4wbvasPL-lybq-rg72-7gyF-So63qtERiKXt");var subQ2=makeQuery(id+"F0.imprint","INTERSECT",VERTEX,{"disambiguationData":[OD(0.0)],"derivedFrom":[subQ1,subQ0]});Q39=makeQuery(id+"F0.imprint","IMPRINT",FACE,{"disambiguationData":[TD([[makeQuery(id+"F0.imprint","IMPRINT",EDGE,{"disambiguationData":[TD([[subQ2,-1.0]])],"derivedFrom":subQ1}),-1.0]])]});}
            extrude(context, id + "F1", {"entities" : qUnion([Q0, Q1, Q2, Q3, Q4, Q5, Q6, Q7, Q8, Q9, Q10, Q11, Q12, Q13, Q14, Q15, Q16, Q17, Q18, Q19, Q20, Q21, Q22, Q23, Q24, Q25, Q26, Q27, Q28, Q29, Q30, Q31, Q32, Q33, Q34, Q35, Q36, Q37, Q38, Q39]), "endBound" : BoundingType.SYMMETRIC, "depth" : 9.65 * mm, "offsetDistance" : 25.4 * mm});
        }
        {
            var Q0;
            {var subQ5=sQuery(id+"F0.wireOp",EDGE,"E0.right");Q0=makeQuery(id+"F0.imprint","IMPRINT",FACE,{"disambiguationData":[TD([[makeQuery(id+"F0.imprint","IMPRINT",EDGE,{"derivedFrom":subQ5}),-1.0]])]});}
            var Q1;
            {var subQ0=sQuery(id+"F0.wireOp",EDGE,"RLhMJPxt-T0ks-Q18N-HPs9-RlDWo5XNaPYv");var subQ1=sQuery(id+"F0.wireOp",EDGE,"yNH20HZv-yYwh-2LKZ-svyh-G2NepNTWeq7k");var subQ2=makeQuery(id+"F0.imprint","INTERSECT",VERTEX,{"derivedFrom":[subQ1,subQ0]});Q1=makeQuery(id+"F0.imprint","IMPRINT",FACE,{"disambiguationData":[TD([[makeQuery(id+"F0.imprint","IMPRINT",EDGE,{"disambiguationData":[TD([[subQ2,-1.0]])],"derivedFrom":subQ1}),-1.0]])]});}
            var Q2;
            {var subQ1=sQuery(id+"F0.wireOp",EDGE,"5da51b9d-8d32-4ced-8ef7-5cde5154bd8f");var subQ2=sQuery(id+"F0.wireOp",EDGE,"c4sJ5hHI-HrM4-fpc8-U7ZW-TC2As1xjlsWM");var subQ4=makeQuery(id+"F0.imprint","INTERSECT",VERTEX,{"derivedFrom":[subQ2,subQ1]});Q2=makeQuery(id+"F0.imprint","IMPRINT",FACE,{"disambiguationData":[TD([[makeQuery(id+"F0.imprint","IMPRINT",EDGE,{"disambiguationData":[TD([[subQ4,1.0]])],"derivedFrom":subQ2}),1.0]])]});}
            var Q3;
            {var subQ0=sQuery(id+"F0.wireOp",EDGE,"peL5V59j-W3Fm-Zrhc-VtZz-2UojcVPXmRrK");Q3=makeQuery(id+"F0.imprint","IMPRINT",FACE,{"disambiguationData":[TD([[makeQuery(id+"F0.imprint","IMPRINT",EDGE,{"derivedFrom":subQ0}),1.0]])]});}
            var Q4;
            {var subQ0=sQuery(id+"F0.wireOp",EDGE,"LmnLbVww-3afu-He10-9RXc-WreO13YMfzCI");Q4=makeQuery(id+"F0.imprint","IMPRINT",FACE,{"disambiguationData":[TD([[makeQuery(id+"F0.imprint","IMPRINT",EDGE,{"derivedFrom":subQ0}),-1.0]])]});}
            var Q5;
            {var subQ0=sQuery(id+"F0.wireOp",EDGE,"7ZUbd3QP-PnaX-XHT3-iJIz-UabsuwuRj2bz");Q5=makeQuery(id+"F0.imprint","IMPRINT",FACE,{"disambiguationData":[TD([[makeQuery(id+"F0.imprint","IMPRINT",EDGE,{"derivedFrom":subQ0}),1.0]])]});}
            var Q6;
            {var subQ0=sQuery(id+"F0.wireOp",EDGE,"n1DMEA80-rfYu-xhKm-7zf1-Dh5WKcBCfZ8q");Q6=makeQuery(id+"F0.imprint","IMPRINT",FACE,{"disambiguationData":[TD([[makeQuery(id+"F0.imprint","IMPRINT",EDGE,{"derivedFrom":subQ0}),-1.0]])]});}
            var Q7;
            {var subQ0=sQuery(id+"F0.wireOp",EDGE,"hjrOhq4C-YDQ2-2L1C-Vmbz-qUVbdpo7c3ap");Q7=makeQuery(id+"F0.imprint","IMPRINT",FACE,{"disambiguationData":[TD([[makeQuery(id+"F0.imprint","IMPRINT",EDGE,{"derivedFrom":subQ0}),1.0]])]});}
            var Q8;
            {var subQ2=sQuery(id+"F0.wireOp",EDGE,"hjrOhq4C-YDQ2-2L1C-Vmbz-qUVbdpo7c3ap");Q8=makeQuery(id+"F0.imprint","IMPRINT",FACE,{"disambiguationData":[TD([[makeQuery(id+"F0.imprint","IMPRINT",EDGE,{"derivedFrom":subQ2}),-1.0]])]});}
            var Q9;
            {var subQ2=sQuery(id+"F0.wireOp",EDGE,"nO7gmJ5v-JFEN-2ivU-SbOD-OSDMOO5U7c10");Q9=makeQuery(id+"F0.imprint","IMPRINT",FACE,{"disambiguationData":[TD([[makeQuery(id+"F0.imprint","IMPRINT",EDGE,{"derivedFrom":subQ2}),1.0]])]});}
            var Q10;
            {var subQ0=sQuery(id+"F0.wireOp",EDGE,"cJxqukpS-sKDF-N0Gn-XzKz-uhADJrMwIFSU");Q10=makeQuery(id+"F0.imprint","IMPRINT",FACE,{"disambiguationData":[TD([[makeQuery(id+"F0.imprint","IMPRINT",EDGE,{"derivedFrom":subQ0}),1.0]])]});}
            var Q11;
            {var subQ0=sQuery(id+"F0.wireOp",EDGE,"cJxqukpS-sKDF-N0Gn-XzKz-uhADJrMwIFSU");Q11=makeQuery(id+"F0.imprint","IMPRINT",FACE,{"disambiguationData":[TD([[makeQuery(id+"F0.imprint","IMPRINT",EDGE,{"derivedFrom":subQ0}),-1.0]])]});}
            var Q12;
            {var subQ3=sQuery(id+"F0.wireOp",EDGE,"8bbff9a0-f29a-4255-a7a3-932c1e6babc1.1");var subQ5=sQuery(id+"F0.wireOp",EDGE,"8bbff9a0-f29a-4255-a7a3-932c1e6babc1.2");var subQ6=makeQuery(id+"F0.imprint","INTERSECT",VERTEX,{"derivedFrom":[subQ3,subQ5]});Q12=makeQuery(id+"F0.imprint","IMPRINT",FACE,{"disambiguationData":[TD([[makeQuery(id+"F0.imprint","IMPRINT",EDGE,{"disambiguationData":[TD([[subQ6,1.0]])],"derivedFrom":subQ3}),1.0]])]});}
            var Q13;
            {var subQ0=sQuery(id+"F0.wireOp",EDGE,"E9");Q13=makeQuery(id+"F0.imprint","IMPRINT",FACE,{"disambiguationData":[TD([[makeQuery(id+"F0.imprint","IMPRINT",EDGE,{"derivedFrom":subQ0}),-1.0]])]});}
            var Q14;
            {var subQ0=sQuery(id+"F0.wireOp",EDGE,"E10");Q14=makeQuery(id+"F0.imprint","IMPRINT",FACE,{"disambiguationData":[TD([[makeQuery(id+"F0.imprint","IMPRINT",EDGE,{"derivedFrom":subQ0}),-1.0]])]});}
            var Q15;
            {var subQ0=sQuery(id+"F0.wireOp",EDGE,"E33");var subQ4=sQuery(id+"F0.wireOp",EDGE,"E20");var subQ7=makeQuery(id+"F0.imprint","INTERSECT",VERTEX,{"derivedFrom":[subQ4,subQ0]});Q15=makeQuery(id+"F0.imprint","IMPRINT",FACE,{"disambiguationData":[TD([[makeQuery(id+"F0.imprint","IMPRINT",EDGE,{"disambiguationData":[TD([[subQ7,1.0]])],"derivedFrom":subQ4}),-1.0]])]});}
            var Q16;
            {var subQ0=sQuery(id+"F0.wireOp",EDGE,"E32");Q16=makeQuery(id+"F0.imprint","IMPRINT",FACE,{"disambiguationData":[TD([[makeQuery(id+"F0.imprint","IMPRINT",EDGE,{"derivedFrom":subQ0}),-1.0]])]});}
            var Q17;
            {var subQ0=sQuery(id+"F0.wireOp",EDGE,"95b7a578-6bee-43eb-946b-d34cbbbfe364");var subQ1=sQuery(id+"F0.wireOp",EDGE,"HR7Vcqbq-5GC2-dnc4-iXz6-dvDuRuYr12mq");var subQ2=makeQuery(id+"F0.imprint","INTERSECT",VERTEX,{"disambiguationData":[OD(2.0)],"derivedFrom":[subQ1,subQ0]});Q17=makeQuery(id+"F0.imprint","IMPRINT",FACE,{"disambiguationData":[TD([[makeQuery(id+"F0.imprint","IMPRINT",EDGE,{"disambiguationData":[TD([[subQ2,-1.0]])],"derivedFrom":subQ1}),-1.0]])]});}
            var Q18;
            {var subQ0=sQuery(id+"F0.wireOp",EDGE,"95b7a578-6bee-43eb-946b-d34cbbbfe364");var subQ1=sQuery(id+"F0.wireOp",EDGE,"xbz5I5cg-mLEk-vWxP-3GDN-i6KnoVRDJ0Sn");var subQ2=makeQuery(id+"F0.imprint","INTERSECT",VERTEX,{"derivedFrom":[subQ1,subQ0]});Q18=makeQuery(id+"F0.imprint","IMPRINT",FACE,{"disambiguationData":[TD([[makeQuery(id+"F0.imprint","IMPRINT",EDGE,{"disambiguationData":[TD([[subQ2,1.0]])],"derivedFrom":subQ1}),-1.0]])]});}
            var Q19;
            {var subQ0=sQuery(id+"F0.wireOp",EDGE,"95b7a578-6bee-43eb-946b-d34cbbbfe364");var subQ1=sQuery(id+"F0.wireOp",EDGE,"xbz5I5cg-mLEk-vWxP-3GDN-i6KnoVRDJ0Sn");var subQ2=makeQuery(id+"F0.imprint","INTERSECT",VERTEX,{"derivedFrom":[subQ1,subQ0]});Q19=makeQuery(id+"F0.imprint","IMPRINT",FACE,{"disambiguationData":[TD([[makeQuery(id+"F0.imprint","IMPRINT",EDGE,{"disambiguationData":[TD([[subQ2,1.0]])],"derivedFrom":subQ1}),1.0]])]});}
            extrude(context, id + "F2", {"entities" : qUnion([Q0, Q1, Q2, Q3, Q4, Q5, Q6, Q7, Q8, Q9, Q10, Q11, Q12, Q13, Q14, Q15, Q16, Q17, Q18, Q19]), "endBound" : BoundingType.SYMMETRIC, "depth" : 5.08 * mm, "offsetDistance" : 25.4 * mm});
        }
        {
            var Q0;
            {var subQ3=sQuery(id+"F0.wireOp",EDGE,"PweVwEmF-89VC-OnO4-D6vt-i3SsO2vePyoG");Q0=makeQuery(id+"F0.imprint","IMPRINT",FACE,{"disambiguationData":[TD([[makeQuery(id+"F0.imprint","IMPRINT",EDGE,{"derivedFrom":subQ3}),1.0]])]});}
            var Q1;
            {var subQ0=sQuery(id+"F0.wireOp",EDGE,"077caab9-3edd-4d49-a446-deb494107614");var subQ1=sQuery(id+"F0.wireOp",EDGE,"oO86CIyH-V04x-DpEi-sI8J-O24Eu7E0Mc1g");var subQ3=makeQuery(id+"F0.imprint","INTERSECT",VERTEX,{"disambiguationData":[OD(0.0)],"derivedFrom":[subQ1,subQ0]});Q1=makeQuery(id+"F0.imprint","IMPRINT",FACE,{"disambiguationData":[TD([[makeQuery(id+"F0.imprint","IMPRINT",EDGE,{"disambiguationData":[TD([[subQ3,1.0]])],"derivedFrom":subQ1}),1.0]])]});}
            var Q2;
            {var subQ3=sQuery(id+"F0.wireOp",EDGE,"rIkObhGf-iI1Q-mgAK-UAuT-PYoezx3TNEve");var subQ6=sQuery(id+"F0.wireOp",EDGE,"t13odgRn-F5jQ-I7TH-b6EP-mQaY1AUBK2Dm");var subQ8=makeQuery(id+"F0.imprint","INTERSECT",VERTEX,{"derivedFrom":[subQ3,subQ6]});Q2=makeQuery(id+"F0.imprint","IMPRINT",FACE,{"disambiguationData":[TD([[makeQuery(id+"F0.imprint","IMPRINT",EDGE,{"disambiguationData":[TD([[subQ8,1.0]])],"derivedFrom":subQ3}),-1.0]])]});}
            var Q3;
            {var subQ0=sQuery(id+"F0.wireOp",EDGE,"077caab9-3edd-4d49-a446-deb494107614");var subQ1=sQuery(id+"F0.wireOp",EDGE,"oO86CIyH-V04x-DpEi-sI8J-O24Eu7E0Mc1g");var subQ3=makeQuery(id+"F0.imprint","INTERSECT",VERTEX,{"disambiguationData":[OD(1.0)],"derivedFrom":[subQ1,subQ0]});Q3=makeQuery(id+"F0.imprint","IMPRINT",FACE,{"disambiguationData":[TD([[makeQuery(id+"F0.imprint","IMPRINT",EDGE,{"disambiguationData":[TD([[subQ3,-1.0]])],"derivedFrom":subQ1}),1.0]])]});}
            var Q4;
            {var subQ0=sQuery(id+"F0.wireOp",EDGE,"t13odgRn-F5jQ-I7TH-b6EP-mQaY1AUBK2Dm");var subQ1=sQuery(id+"F0.wireOp",EDGE,"rIkObhGf-iI1Q-mgAK-UAuT-PYoezx3TNEve");var subQ2=makeQuery(id+"F0.imprint","INTERSECT",VERTEX,{"derivedFrom":[subQ1,subQ0]});Q4=makeQuery(id+"F0.imprint","IMPRINT",FACE,{"disambiguationData":[TD([[makeQuery(id+"F0.imprint","IMPRINT",EDGE,{"disambiguationData":[TD([[subQ2,1.0]])],"derivedFrom":subQ1}),1.0]])]});}
            var Q5;
            {var subQ3=sQuery(id+"F0.wireOp",EDGE,"94QjObYg-kscN-IWlI-6DmT-E6O7HMAgr5X8");var subQ6=sQuery(id+"F0.wireOp",EDGE,"djvSYdSa-Qz4f-1sGb-zx6T-8l97WevlQRFn");var subQ8=makeQuery(id+"F0.imprint","INTERSECT",VERTEX,{"derivedFrom":[subQ6,subQ3]});Q5=makeQuery(id+"F0.imprint","IMPRINT",FACE,{"disambiguationData":[TD([[makeQuery(id+"F0.imprint","IMPRINT",EDGE,{"disambiguationData":[TD([[subQ8,1.0]])],"derivedFrom":subQ6}),-1.0]])]});}
            var Q6;
            {var subQ0=sQuery(id+"F0.wireOp",EDGE,"94QjObYg-kscN-IWlI-6DmT-E6O7HMAgr5X8");var subQ1=sQuery(id+"F0.wireOp",EDGE,"djvSYdSa-Qz4f-1sGb-zx6T-8l97WevlQRFn");var subQ2=makeQuery(id+"F0.imprint","INTERSECT",VERTEX,{"derivedFrom":[subQ1,subQ0]});Q6=makeQuery(id+"F0.imprint","IMPRINT",FACE,{"disambiguationData":[TD([[makeQuery(id+"F0.imprint","IMPRINT",EDGE,{"disambiguationData":[TD([[subQ2,1.0]])],"derivedFrom":subQ1}),1.0]])]});}
            var Q7;
            {var subQ0=sQuery(id+"F0.wireOp",EDGE,"f45a8b09-8381-489b-a60a-99bbd61589e0");var subQ1=sQuery(id+"F0.wireOp",EDGE,"4wbvasPL-lybq-rg72-7gyF-So63qtERiKXt");var subQ3=makeQuery(id+"F0.imprint","INTERSECT",VERTEX,{"disambiguationData":[OD(1.0)],"derivedFrom":[subQ1,subQ0]});Q7=makeQuery(id+"F0.imprint","IMPRINT",FACE,{"disambiguationData":[TD([[makeQuery(id+"F0.imprint","IMPRINT",EDGE,{"disambiguationData":[TD([[subQ3,-1.0]])],"derivedFrom":subQ1}),1.0]])]});}
            var Q8;
            {var subQ0=sQuery(id+"F0.wireOp",EDGE,"f45a8b09-8381-489b-a60a-99bbd61589e0");var subQ1=sQuery(id+"F0.wireOp",EDGE,"4wbvasPL-lybq-rg72-7gyF-So63qtERiKXt");var subQ3=makeQuery(id+"F0.imprint","INTERSECT",VERTEX,{"disambiguationData":[OD(0.0)],"derivedFrom":[subQ1,subQ0]});Q8=makeQuery(id+"F0.imprint","IMPRINT",FACE,{"disambiguationData":[TD([[makeQuery(id+"F0.imprint","IMPRINT",EDGE,{"disambiguationData":[TD([[subQ3,1.0]])],"derivedFrom":subQ1}),1.0]])]});}
            var Q9;
            {var subQ3=sQuery(id+"F0.wireOp",EDGE,"kEbFNsaM-hIZe-opiU-NVuC-8ptyRgOxsJVG");Q9=makeQuery(id+"F0.imprint","IMPRINT",FACE,{"disambiguationData":[TD([[makeQuery(id+"F0.imprint","IMPRINT",EDGE,{"derivedFrom":subQ3}),1.0]])]});}
            var Q10;
            {var subQ4=sQuery(id+"F0.wireOp",EDGE,"E0.left");Q10=makeQuery(id+"F0.imprint","IMPRINT",FACE,{"disambiguationData":[TD([[makeQuery(id+"F0.imprint","IMPRINT",EDGE,{"derivedFrom":subQ4}),-1.0]])]});}
            extrude(context, id + "F3", {"entities" : qUnion([Q0, Q1, Q2, Q3, Q4, Q5, Q6, Q7, Q8, Q9, Q10]), "endBound" : BoundingType.SYMMETRIC, "depth" : 8.64 * mm, "offsetDistance" : 25.4 * mm});
        }
        {
            var Q0;
            {var subQ8=sQuery(id+"F0.wireOp",EDGE,"E12");Q0=makeQuery(id+"F0.imprint","IMPRINT",FACE,{"disambiguationData":[TD([[makeQuery(id+"F0.imprint","IMPRINT",EDGE,{"derivedFrom":subQ8}),-1.0]])]});}
            extrude(context, id + "F4", {"entities" : qUnion([Q0]), "endBound" : BoundingType.SYMMETRIC, "depth" : 1.02 * mm, "offsetDistance" : 25.4 * mm});
        }
        {
            var Q0;
            Q0=makeQuery(id+"F0.imprint","IMPRINT",FACE,{"disambiguationData":[TD([[makeQuery(id+"F0.imprint","IMPRINT",EDGE,{"derivedFrom":sQuery(id+"F0.wireOp",EDGE,"E34")}),1.0]])]});
            var Q1;
            Q1=makeQuery(id+"F0.imprint","IMPRINT",FACE,{"disambiguationData":[TD([[makeQuery(id+"F0.imprint","IMPRINT",EDGE,{"derivedFrom":sQuery(id+"F0.wireOp",EDGE,"E38")}),1.0]])]});
            extrude(context, id + "F5", {"entities" : qUnion([Q0, Q1]), "operationType" : NewBodyOperationType.ADD, "depth" : 7.62 * mm, "offsetDistance" : 25.4 * mm});
        }
    });
